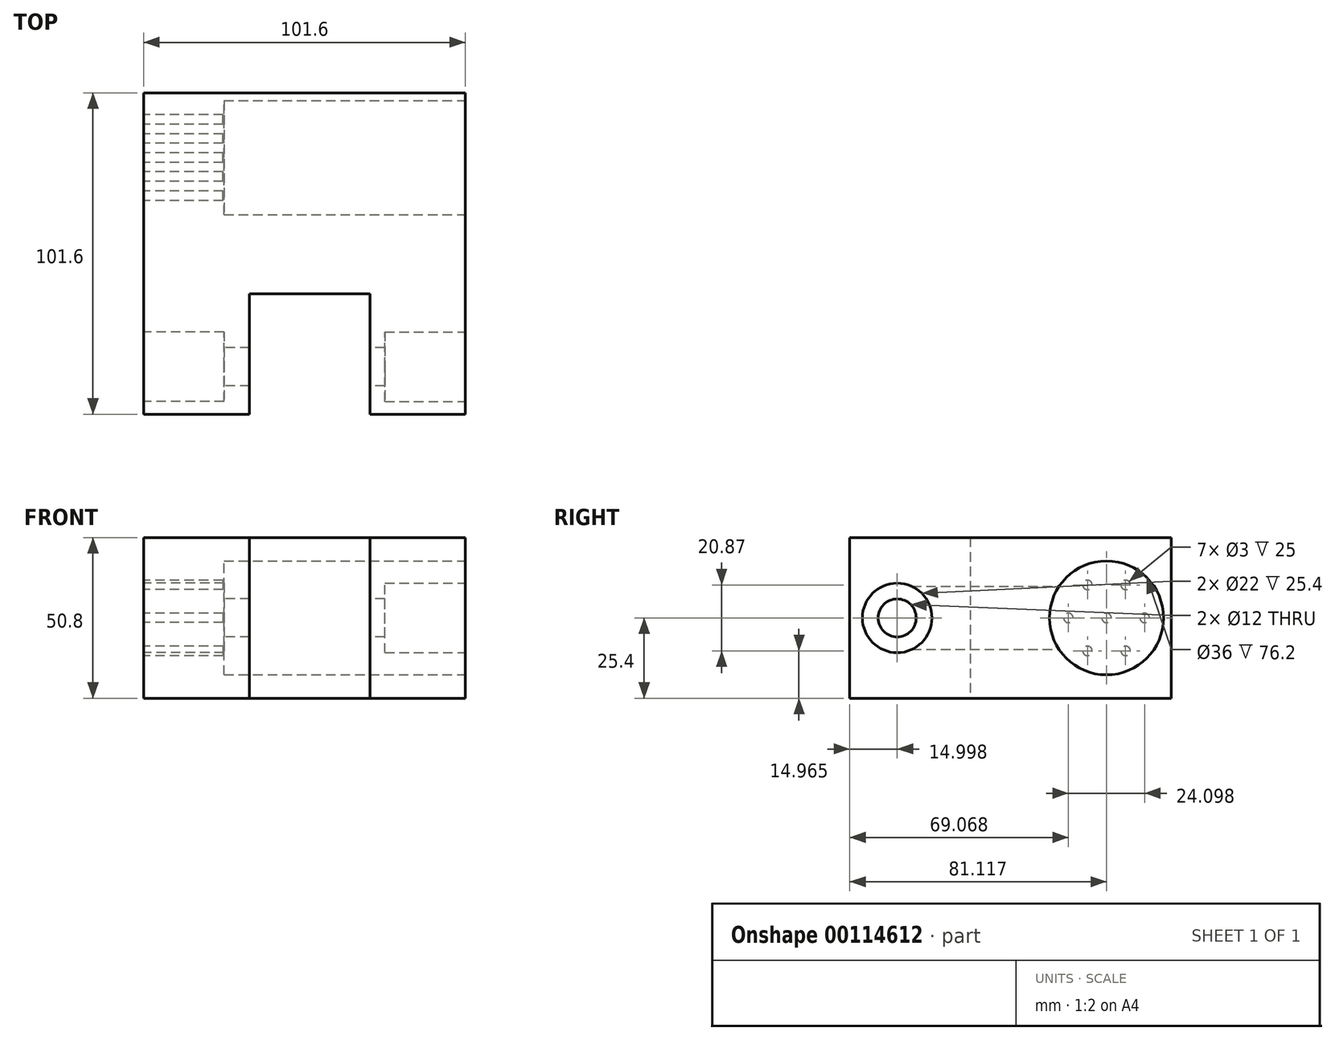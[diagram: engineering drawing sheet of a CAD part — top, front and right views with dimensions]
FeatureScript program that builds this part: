
annotation { "Feature Type Name" : "Feature", "Feature Type Description" : "" }
export const myFeature = defineFeature(function(context is Context, id is Id, definition is map)
    precondition{}
    {
        {
            var Q0;
            Q0=qCreatedBy(makeId("Top.planeOp"),FACE);
            var sketch = newSketch(context, id + "F0", { "sketchPlane" : qUnion([Q0])});
            skLineSegment(sketch, "E0.bottom", {"start": v(-52.5, -59.23) * mm, "end": v(49.1, -59.23) * mm});
            skLineSegment(sketch, "E0.top", {"start": v(-52.5, 42.37) * mm, "end": v(49.1, 42.37) * mm});
            skLineSegment(sketch, "E0.left", {"start": v(-52.5, -59.23) * mm, "end": v(-52.5, 42.37) * mm});
            skLineSegment(sketch, "E0.right", {"start": v(49.1, -59.23) * mm, "end": v(49.1, 42.37) * mm});
            skSolve(sketch);
        }
        {
            var Q0;
            Q0 = qSketchRegion(id + "F0", true);
            extrude(context, id + "F1", {"entities" : qUnion([Q0]), "endBound" : BoundingType.SYMMETRIC, "depth" : 50.8 * mm});
        }
        {
            var Q0;
            Q0=makeQuery(id+"F1.opExtrude","SWEPT_FACE",FACE,{"disambiguationData":[OSD([sQuery(id+"F0.wireOp",EDGE,"E0.right")])]});
            var sketch = newSketch(context, id + "F2", { "sketchPlane" : qUnion([Q0])});
            skCircle(sketch, "E1", {"center": v(21.89, 0) * mm, "radius": 18 * mm});
            skSolve(sketch);
        }
        {
            var Q0;
            Q0 = qSketchRegion(id + "F2", true);
            extrude(context, id + "F3", {"entities" : qUnion([Q0]), "operationType" : NewBodyOperationType.REMOVE, "oppositeDirection" : true, "depth" : 76.2 * mm});
        }
        {
            var Q0;
            Q0=makeQuery(id+"F1.opExtrude","SWEPT_FACE",FACE,{"disambiguationData":[OSD([sQuery(id+"F0.wireOp",EDGE,"E0.left")])]});
            var sketch = newSketch(context, id + "F4", { "sketchPlane" : qUnion([Q0])});
            skCircle(sketch, "E2.0", {"center": v(-21.89, 0) * mm, "radius": 18 * mm});
            skSolve(sketch);
        }
        {
            var Q0;
            Q0 = qSketchRegion(id + "F4", true);
            extrude(context, id + "F5", {"entities" : qUnion([Q0]), "operationType" : NewBodyOperationType.REMOVE, "oppositeDirection" : true, "depth" : 3 / 101.6 * mm});
        }
        {
            var Q0;
            Q0=makeQuery(id+"F5.boolean.opBoolean","COPY",FACE,{"derivedFrom":makeQuery(id+"F5.opExtrude","CAP_FACE",FACE,{"disambiguationData":[OSD([sQuery(id+"F4.wireOp",EDGE,"E2.0")])],"isStart":false})});
            var sketch = newSketch(context, id + "F6", { "sketchPlane" : qUnion([Q0])});
            skCircle(sketch, "E3", {"center": v(-21.89, 0) * mm, "radius": 1.5 * mm});
            skCircle(sketch, "E4", {"center": v(-9.84, 0) * mm, "radius": 1.5 * mm});
            skCircle(sketch, "E5.1.0", {"center": v(-15.86, 10.43) * mm, "radius": 1.5 * mm});
            skCircle(sketch, "E5.2.0", {"center": v(-27.91, 10.43) * mm, "radius": 1.5 * mm});
            skCircle(sketch, "E5.3.0", {"center": v(-33.94, 0) * mm, "radius": 1.5 * mm});
            skCircle(sketch, "E5.4.0", {"center": v(-27.91, -10.43) * mm, "radius": 1.5 * mm});
            skCircle(sketch, "E5.5.0", {"center": v(-15.86, -10.43) * mm, "radius": 1.5 * mm});
            skSolve(sketch);
        }
        {
            var Q0;
            Q0 = qSketchRegion(id + "F6", true);
            extrude(context, id + "F7", {"entities" : qUnion([Q0]), "operationType" : NewBodyOperationType.REMOVE, "oppositeDirection" : true, "depth" : 25 * mm});
        }
        {
            var Q0;
            Q0=makeQuery(id+"F1.opExtrude","SWEPT_FACE",FACE,{"disambiguationData":[OSD([sQuery(id+"F0.wireOp",EDGE,"E0.left")])]});
            var sketch = newSketch(context, id + "F8", { "sketchPlane" : qUnion([Q0])});
            skCircle(sketch, "E6", {"center": v(44.23, 0) * mm, "radius": 11 * mm});
            skSolve(sketch);
        }
        {
            var Q0;
            Q0 = qSketchRegion(id + "F8", true);
            extrude(context, id + "F9", {"entities" : qUnion([Q0]), "operationType" : NewBodyOperationType.REMOVE, "oppositeDirection" : true, "depth" : 25.4 * mm});
        }
        {
            var Q0;
            Q0=makeQuery(id+"F1.opExtrude","SWEPT_FACE",FACE,{"disambiguationData":[OSD([sQuery(id+"F0.wireOp",EDGE,"E0.right")])]});
            var sketch = newSketch(context, id + "F10", { "sketchPlane" : qUnion([Q0])});
            skCircle(sketch, "E7.0", {"center": v(-44.23, 0) * mm, "radius": 11 * mm});
            skSolve(sketch);
        }
        {
            var Q0;
            Q0 = qSketchRegion(id + "F10", true);
            extrude(context, id + "F11", {"entities" : qUnion([Q0]), "operationType" : NewBodyOperationType.REMOVE, "oppositeDirection" : true, "depth" : 25.4 * mm});
        }
        {
            var Q0;
            Q0=makeQuery(id+"F1.opExtrude","CAP_FACE",FACE,{"disambiguationData":[OSD([sQuery(id+"F0.wireOp",EDGE,"E0.bottom"),sQuery(id+"F0.wireOp",EDGE,"E0.top"),sQuery(id+"F0.wireOp",EDGE,"E0.left"),sQuery(id+"F0.wireOp",EDGE,"E0.right")])],"isStart":true});
            var sketch = newSketch(context, id + "F12", { "sketchPlane" : qUnion([Q0])});
            skLineSegment(sketch, "E8.bottom", {"start": v(-19.05, 64.5) * mm, "end": v(19.05, 64.5) * mm});
            skLineSegment(sketch, "E8.top", {"start": v(-19.05, 21.13) * mm, "end": v(19.05, 21.13) * mm});
            skLineSegment(sketch, "E8.left", {"start": v(-19.05, 64.5) * mm, "end": v(-19.05, 21.13) * mm});
            skLineSegment(sketch, "E8.right", {"start": v(19.05, 64.5) * mm, "end": v(19.05, 21.13) * mm});
            skSolve(sketch);
        }
        {
            var Q0;
            Q0 = qSketchRegion(id + "F12", true);
            extrude(context, id + "F13", {"entities" : qUnion([Q0]), "operationType" : NewBodyOperationType.REMOVE, "endBound" : BoundingType.THROUGH_ALL, "oppositeDirection" : true, "depth" : 25 * mm});
        }
        {
            var Q0;
            Q0=makeQuery(id+"F9.boolean.opBoolean","COPY",FACE,{"derivedFrom":makeQuery(id+"F9.opExtrude","CAP_FACE",FACE,{"disambiguationData":[OSD([sQuery(id+"F8.wireOp",EDGE,"E6")])],"isStart":false})});
            var sketch = newSketch(context, id + "F14", { "sketchPlane" : qUnion([Q0])});
            skCircle(sketch, "E9", {"center": v(44.23, 0) * mm, "radius": 6 * mm});
            skSolve(sketch);
        }
        {
            var Q0;
            Q0 = qSketchRegion(id + "F14", true);
            extrude(context, id + "F15", {"entities" : qUnion([Q0]), "operationType" : NewBodyOperationType.REMOVE, "endBound" : BoundingType.THROUGH_ALL, "oppositeDirection" : true, "depth" : 25 * mm});
        }
        {
            var Q0;
            Q0=makeQuery(id+"F1.opExtrude","SWEPT_FACE",FACE,{"disambiguationData":[OSD([sQuery(id+"F0.wireOp",EDGE,"E0.left")])]});
            var sketch = newSketch(context, id + "F16", { "sketchPlane" : qUnion([Q0])});
            skArc(sketch, "E10", {"start": v(44.23, -10) * mm, "mid": v(54.23, 0) * mm, "end": v(44.23, 10) * mm});
            skArc(sketch, "E11", {"start": v(-21.89, 10) * mm, "mid": v(-31.89, 0) * mm, "end": v(-21.89, -10) * mm});
            skLineSegment(sketch, "E12", {"start": v(44.23, 10) * mm, "end": v(-21.89, 10) * mm});
            skLineSegment(sketch, "E13", {"start": v(44.23, -10) * mm, "end": v(-21.89, -10) * mm});
            skSolve(sketch);
        }
        {
            var Q0;
            Q0 = qSketchRegion(id + "F16", true);
            extrude(context, id + "F17", {"entities" : qUnion([Q0]), "operationType" : NewBodyOperationType.REMOVE, "oppositeDirection" : true, "depth" : 3 / 101.6 * mm});
        }
    });
